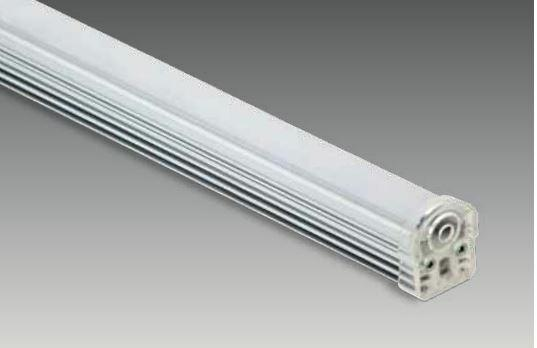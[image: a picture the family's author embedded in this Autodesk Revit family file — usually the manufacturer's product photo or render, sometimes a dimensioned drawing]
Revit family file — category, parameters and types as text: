
# Revit family: SD 0260 CVK
name_source: partatom
category: Lighting Fixtures
revit_build: Autodesk Revit 2017 (Build: 20160225_1515(x64)
units: mm (PartAtom-declared; Revit-internal decimal feet)

## family parameters
Cut with Voids When Loaded = No
Host = Face
Light Source = Yes
Part Type = Normal
Room Calculation Point = No
Round Connector Dimension = Use Diameter
Shared = No

## types (2) — shared parameters
Apparent Load = 6 VA
Color Filter = 16777215
Default Elevation = 1219 mm
Dimming Lamp Color Temperature Shift = <None>
Emit Shape Visible in Rendering = Yes
Emit from Rectangle Length = 250 mm  [stored 0.82021 ft]
Emit from Rectangle Width = 15 mm  [stored 0.0492126 ft]
Light Source Symbol Size = 610 mm
Manufacturer = ARLIGHT
Type Image = SD 0260 CVK.JPG
Wattage Comments = 6

## type names (no varying parameters)
- SDCVK.260.6.30
- SDCVK.260.6.40

note: [stored X ft] marks values corroborated as IEEE doubles in the binary element streams (Revit-internal decimal feet)

## geometry (parser evidence)
native form markers: Sweep x3
no freeform markers — native parametric forms only
